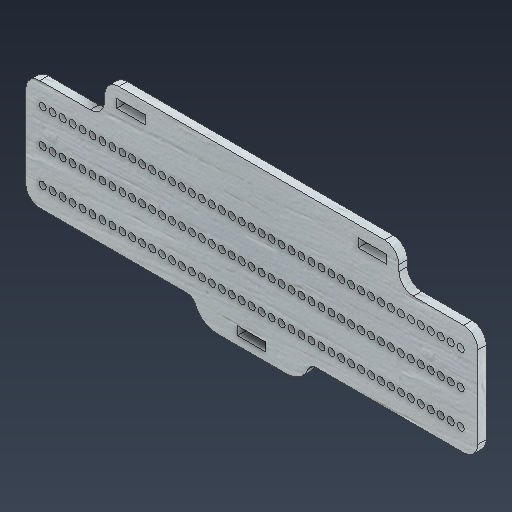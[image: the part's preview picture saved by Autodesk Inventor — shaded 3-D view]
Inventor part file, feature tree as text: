
AUTODESK INVENTOR PART (.ipt)
format: ipt  version: 2025.3 (Build 293356000, 356)  size: 498,176 bytes
history: native  units: mm
features: other x3, sketch x3, extrude x1
ambient origin geometry x8: Origin, YZ Plane, XZ Plane, XY Plane, X Axis, Y Axis, Z Axis, Center Point
bodies: Body1 (feature_tree)
feature tree (7):
  other  "實體1"
  extrude  "擠出1"  Depth=10.0mm
  sketch  "草圖3"
  sketch  "草圖5"
  sketch  "草圖1"
  other  "草圖 - 矩形陣列5"
  other  "草圖 - 矩形陣列12"
